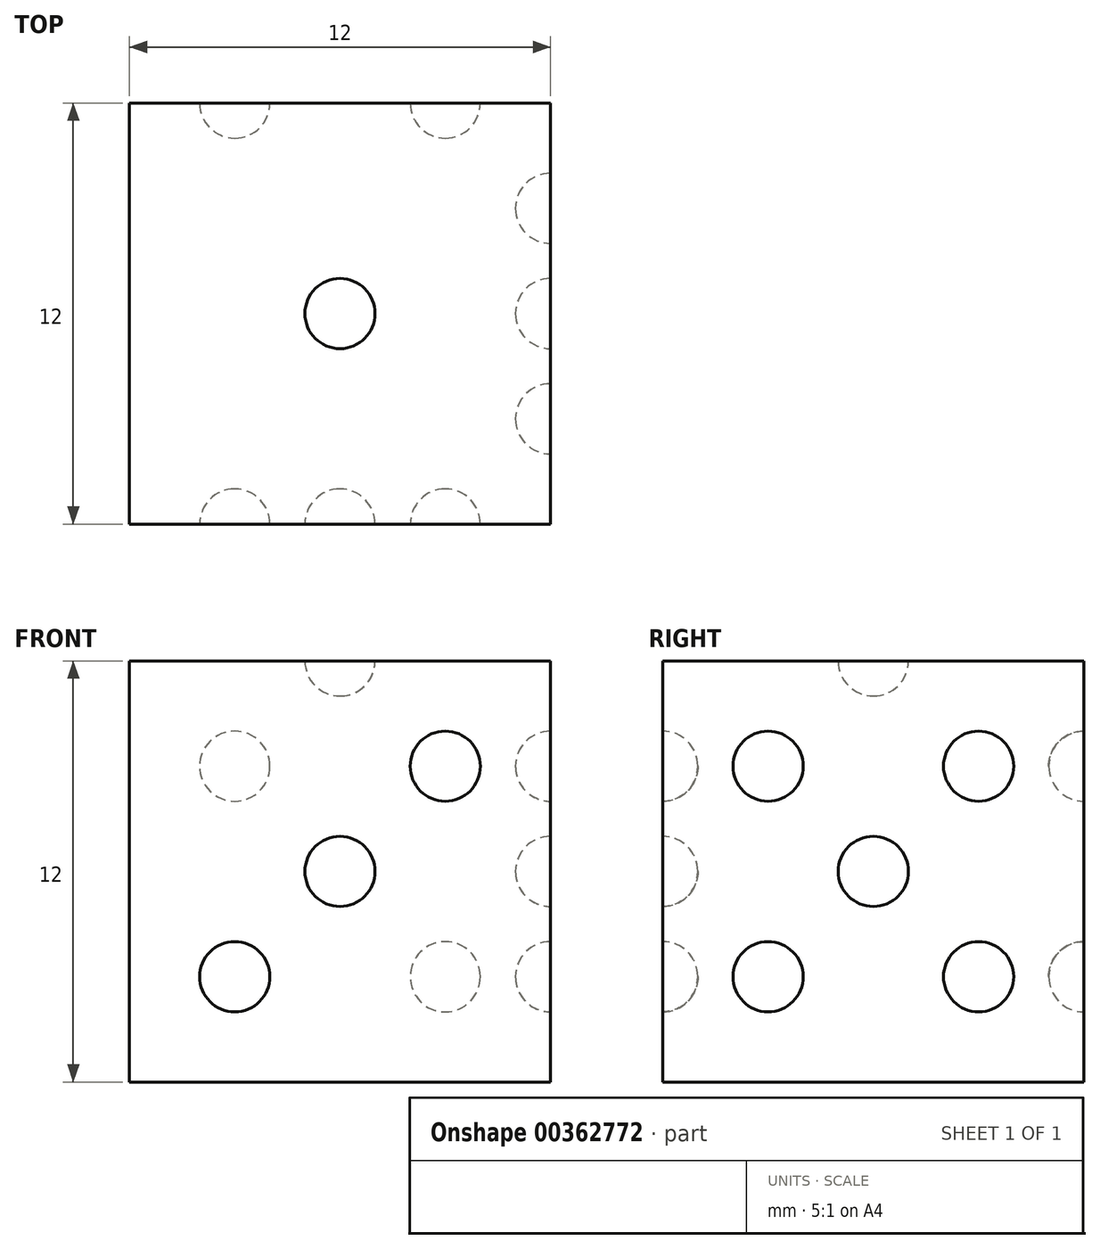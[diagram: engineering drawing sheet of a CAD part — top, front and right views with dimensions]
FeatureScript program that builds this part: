
annotation { "Feature Type Name" : "Feature", "Feature Type Description" : "" }
export const myFeature = defineFeature(function(context is Context, id is Id, definition is map)
    precondition{}
    {
        {
            var Q0;
            Q0=qCreatedBy(makeId("Top.planeOp"),FACE);
            cPlane(context, id + "F0", {"entities" : qUnion([Q0]), "cplaneType" : CPlaneType.OFFSET, "offset" : 6 * mm, "oppositeDirection" : true, "width" : 150 * mm, "height" : 150 * mm});
        }
        {
            var Q0;
            Q0=qCreatedBy(id+"F0.planeOp",FACE);
            var sketch = newSketch(context, id + "F1", { "sketchPlane" : qUnion([Q0])});
            skLineSegment(sketch, "E0.bottom", {"start": v(6, 6) * mm, "end": v(-6, 6) * mm});
            skLineSegment(sketch, "E0.top", {"start": v(6, -6) * mm, "end": v(-6, -6) * mm});
            skLineSegment(sketch, "E0.left", {"start": v(6, 6) * mm, "end": v(6, -6) * mm});
            skLineSegment(sketch, "E0.right", {"start": v(-6, 6) * mm, "end": v(-6, -6) * mm});
            skPoint(sketch, "E0.middle", {"position": v(0, 0) * mm});
            skSolve(sketch);
        }
        {
            var Q0;
            Q0=makeQuery(id+"F1.imprint","IMPRINT",FACE,{"disambiguationData":[TD([[makeQuery(id+"F1.imprint","IMPRINT",EDGE,{"derivedFrom":sQuery(id+"F1.wireOp",EDGE,"E0.bottom")}),1.0]])]});
            extrude(context, id + "F2", {"entities" : qUnion([Q0]), "depth" : 12 * mm});
        }
        {
            var Q0;
            Q0=makeQuery(id+"F2.opExtrude","CAP_FACE",FACE,{"disambiguationData":[OSD([sQuery(id+"F1.wireOp",EDGE,"E0.bottom"),sQuery(id+"F1.wireOp",EDGE,"E0.top"),sQuery(id+"F1.wireOp",EDGE,"E0.left"),sQuery(id+"F1.wireOp",EDGE,"E0.right")])],"isStart":false});
            var sketch = newSketch(context, id + "F3", { "sketchPlane" : qUnion([Q0])});
            skCircle(sketch, "E1", {"center": v(0, 0) * mm, "radius": 1 * mm});
            skSolve(sketch);
        }
        {
            var Q0;
            Q0=makeQuery(id+"F3.imprint","IMPRINT",FACE,{"disambiguationData":[TD([[makeQuery(id+"F3.imprint","IMPRINT",EDGE,{"derivedFrom":sQuery(id+"F3.wireOp",EDGE,"E1")}),1.0]])]});
            extrude(context, id + "F4", {"entities" : qUnion([Q0]), "operationType" : NewBodyOperationType.REMOVE, "oppositeDirection" : true, "depth" : 1 * mm});
        }
        {
            var Q0;
            Q0=makeQuery(id+"F4.boolean.opBoolean","COPY",EDGE,{"derivedFrom":makeQuery(id+"F4.opExtrude","CAP_EDGE",EDGE,{"disambiguationData":[OSD([sQuery(id+"F3.wireOp",EDGE,"E1")])],"isStart":false})});
            fillet(context, id + "F5", {"entities" : qUnion([Q0]), "radius" : 1 * mm, "tangentPropagation" : true, "allowEdgeOverflow" : false});
        }
        {
            var Q0;
            Q0=makeQuery(id+"F2.opExtrude","SWEPT_FACE",FACE,{"disambiguationData":[OSD([sQuery(id+"F1.wireOp",EDGE,"E0.top")])]});
            var sketch = newSketch(context, id + "F6", { "sketchPlane" : qUnion([Q0])});
            skCircle(sketch, "E2", {"center": v(0, 0) * mm, "radius": 1 * mm});
            skPoint(sketch, "E3", {"position": v(3, 3) * mm});
            skCircle(sketch, "E4", {"center": v(3, 3) * mm, "radius": 1 * mm});
            skPoint(sketch, "E5", {"position": v(-3, -3) * mm});
            skCircle(sketch, "E6", {"center": v(-3, -3) * mm, "radius": 1 * mm});
            skSolve(sketch);
        }
        {
            var Q0;
            Q0=makeQuery(id+"F6.imprint","IMPRINT",FACE,{"disambiguationData":[TD([[makeQuery(id+"F6.imprint","IMPRINT",EDGE,{"derivedFrom":sQuery(id+"F6.wireOp",EDGE,"E4")}),1.0]])]});
            var Q1;
            Q1=makeQuery(id+"F6.imprint","IMPRINT",FACE,{"disambiguationData":[TD([[makeQuery(id+"F6.imprint","IMPRINT",EDGE,{"derivedFrom":sQuery(id+"F6.wireOp",EDGE,"E2")}),1.0]])]});
            var Q2;
            Q2=makeQuery(id+"F6.imprint","IMPRINT",FACE,{"disambiguationData":[TD([[makeQuery(id+"F6.imprint","IMPRINT",EDGE,{"derivedFrom":sQuery(id+"F6.wireOp",EDGE,"E6")}),1.0]])]});
            extrude(context, id + "F7", {"entities" : qUnion([Q0, Q1, Q2]), "operationType" : NewBodyOperationType.REMOVE, "oppositeDirection" : true, "depth" : 1 * mm});
        }
        {
            var Q0;
            Q0=makeQuery(id+"F7.boolean.opBoolean","COPY",EDGE,{"derivedFrom":makeQuery(id+"F7.opExtrude","CAP_EDGE",EDGE,{"disambiguationData":[OSD([sQuery(id+"F6.wireOp",EDGE,"E4")])],"isStart":false})});
            var Q1;
            Q1=makeQuery(id+"F7.boolean.opBoolean","COPY",EDGE,{"derivedFrom":makeQuery(id+"F7.opExtrude","CAP_EDGE",EDGE,{"disambiguationData":[OSD([sQuery(id+"F6.wireOp",EDGE,"E2")])],"isStart":false})});
            var Q2;
            Q2=makeQuery(id+"F7.boolean.opBoolean","COPY",EDGE,{"derivedFrom":makeQuery(id+"F7.opExtrude","CAP_EDGE",EDGE,{"disambiguationData":[OSD([sQuery(id+"F6.wireOp",EDGE,"E6")])],"isStart":false})});
            fillet(context, id + "F8", {"entities" : qUnion([Q0, Q1, Q2]), "radius" : 1 * mm, "tangentPropagation" : true, "allowEdgeOverflow" : false});
        }
        {
            var Q0;
            Q0=makeQuery(id+"F2.opExtrude","SWEPT_FACE",FACE,{"disambiguationData":[OSD([sQuery(id+"F1.wireOp",EDGE,"E0.left")])]});
            var sketch = newSketch(context, id + "F9", { "sketchPlane" : qUnion([Q0])});
            skCircle(sketch, "E7", {"center": v(0, 0) * mm, "radius": 1 * mm});
            skPoint(sketch, "E8", {"position": v(3, 3) * mm});
            skPoint(sketch, "E9", {"position": v(-3, -3) * mm});
            skPoint(sketch, "E10", {"position": v(-3, 3) * mm});
            skPoint(sketch, "E11", {"position": v(3, -3) * mm});
            skCircle(sketch, "E12", {"center": v(-3, 3) * mm, "radius": 1 * mm});
            skCircle(sketch, "E13", {"center": v(3, 3) * mm, "radius": 1 * mm});
            skCircle(sketch, "E14", {"center": v(3, -3) * mm, "radius": 1 * mm});
            skCircle(sketch, "E15", {"center": v(-3, -3) * mm, "radius": 1 * mm});
            skSolve(sketch);
        }
        {
            var Q0;
            Q0=makeQuery(id+"F9.imprint","IMPRINT",FACE,{"disambiguationData":[TD([[makeQuery(id+"F9.imprint","IMPRINT",EDGE,{"derivedFrom":sQuery(id+"F9.wireOp",EDGE,"E12")}),1.0]])]});
            var Q1;
            Q1=makeQuery(id+"F9.imprint","IMPRINT",FACE,{"disambiguationData":[TD([[makeQuery(id+"F9.imprint","IMPRINT",EDGE,{"derivedFrom":sQuery(id+"F9.wireOp",EDGE,"E7")}),1.0]])]});
            var Q2;
            Q2=makeQuery(id+"F9.imprint","IMPRINT",FACE,{"disambiguationData":[TD([[makeQuery(id+"F9.imprint","IMPRINT",EDGE,{"derivedFrom":sQuery(id+"F9.wireOp",EDGE,"E13")}),1.0]])]});
            var Q3;
            Q3=makeQuery(id+"F9.imprint","IMPRINT",FACE,{"disambiguationData":[TD([[makeQuery(id+"F9.imprint","IMPRINT",EDGE,{"derivedFrom":sQuery(id+"F9.wireOp",EDGE,"E14")}),1.0]])]});
            var Q4;
            Q4=makeQuery(id+"F9.imprint","IMPRINT",FACE,{"disambiguationData":[TD([[makeQuery(id+"F9.imprint","IMPRINT",EDGE,{"derivedFrom":sQuery(id+"F9.wireOp",EDGE,"E15")}),1.0]])]});
            extrude(context, id + "F10", {"entities" : qUnion([Q0, Q1, Q2, Q3, Q4]), "operationType" : NewBodyOperationType.REMOVE, "oppositeDirection" : true, "depth" : 1 * mm});
        }
        {
            var Q0;
            Q0=makeQuery(id+"F10.boolean.opBoolean","COPY",EDGE,{"derivedFrom":makeQuery(id+"F10.opExtrude","CAP_EDGE",EDGE,{"disambiguationData":[OSD([sQuery(id+"F9.wireOp",EDGE,"E12")])],"isStart":false})});
            var Q1;
            Q1=makeQuery(id+"F10.boolean.opBoolean","COPY",EDGE,{"derivedFrom":makeQuery(id+"F10.opExtrude","CAP_EDGE",EDGE,{"disambiguationData":[OSD([sQuery(id+"F9.wireOp",EDGE,"E7")])],"isStart":false})});
            var Q2;
            Q2=makeQuery(id+"F10.boolean.opBoolean","COPY",EDGE,{"derivedFrom":makeQuery(id+"F10.opExtrude","CAP_EDGE",EDGE,{"disambiguationData":[OSD([sQuery(id+"F9.wireOp",EDGE,"E13")])],"isStart":false})});
            var Q3;
            Q3=makeQuery(id+"F10.boolean.opBoolean","COPY",EDGE,{"derivedFrom":makeQuery(id+"F10.opExtrude","CAP_EDGE",EDGE,{"disambiguationData":[OSD([sQuery(id+"F9.wireOp",EDGE,"E14")])],"isStart":false})});
            var Q4;
            Q4=makeQuery(id+"F10.boolean.opBoolean","COPY",EDGE,{"derivedFrom":makeQuery(id+"F10.opExtrude","CAP_EDGE",EDGE,{"disambiguationData":[OSD([sQuery(id+"F9.wireOp",EDGE,"E15")])],"isStart":false})});
            fillet(context, id + "F11", {"entities" : qUnion([Q0, Q1, Q2, Q3, Q4]), "radius" : 1 * mm, "tangentPropagation" : true, "allowEdgeOverflow" : false});
        }
        {
            var Q0;
            Q0=makeQuery(id+"F2.opExtrude","SWEPT_FACE",FACE,{"disambiguationData":[OSD([sQuery(id+"F1.wireOp",EDGE,"E0.bottom")])]});
            var sketch = newSketch(context, id + "F12", { "sketchPlane" : qUnion([Q0])});
            skCircle(sketch, "E16", {"center": v(-3, 3) * mm, "radius": 1 * mm});
            skCircle(sketch, "E17", {"center": v(3, 3) * mm, "radius": 1 * mm});
            skCircle(sketch, "E18", {"center": v(3, -3) * mm, "radius": 1 * mm});
            skCircle(sketch, "E19", {"center": v(-3, -3) * mm, "radius": 1 * mm});
            skSolve(sketch);
        }
        {
            var Q0;
            Q0=makeQuery(id+"F12.imprint","IMPRINT",FACE,{"disambiguationData":[TD([[makeQuery(id+"F12.imprint","IMPRINT",EDGE,{"derivedFrom":sQuery(id+"F12.wireOp",EDGE,"E16")}),1.0]])]});
            var Q1;
            Q1=makeQuery(id+"F12.imprint","IMPRINT",FACE,{"disambiguationData":[TD([[makeQuery(id+"F12.imprint","IMPRINT",EDGE,{"derivedFrom":sQuery(id+"F12.wireOp",EDGE,"E17")}),1.0]])]});
            var Q2;
            Q2=makeQuery(id+"F12.imprint","IMPRINT",FACE,{"disambiguationData":[TD([[makeQuery(id+"F12.imprint","IMPRINT",EDGE,{"derivedFrom":sQuery(id+"F12.wireOp",EDGE,"E18")}),1.0]])]});
            var Q3;
            Q3=makeQuery(id+"F12.imprint","IMPRINT",FACE,{"disambiguationData":[TD([[makeQuery(id+"F12.imprint","IMPRINT",EDGE,{"derivedFrom":sQuery(id+"F12.wireOp",EDGE,"E19")}),1.0]])]});
            extrude(context, id + "F13", {"entities" : qUnion([Q0, Q1, Q2, Q3]), "operationType" : NewBodyOperationType.REMOVE, "oppositeDirection" : true, "depth" : 1 * mm});
        }
        {
            var Q0;
            Q0=makeQuery(id+"F13.boolean.opBoolean","COPY",EDGE,{"derivedFrom":makeQuery(id+"F13.opExtrude","CAP_EDGE",EDGE,{"disambiguationData":[OSD([sQuery(id+"F12.wireOp",EDGE,"E16")])],"isStart":false})});
            var Q1;
            Q1=makeQuery(id+"F13.boolean.opBoolean","COPY",EDGE,{"derivedFrom":makeQuery(id+"F13.opExtrude","CAP_EDGE",EDGE,{"disambiguationData":[OSD([sQuery(id+"F12.wireOp",EDGE,"E17")])],"isStart":false})});
            var Q2;
            Q2=makeQuery(id+"F13.boolean.opBoolean","COPY",EDGE,{"derivedFrom":makeQuery(id+"F13.opExtrude","CAP_EDGE",EDGE,{"disambiguationData":[OSD([sQuery(id+"F12.wireOp",EDGE,"E19")])],"isStart":false})});
            var Q3;
            Q3=makeQuery(id+"F13.boolean.opBoolean","COPY",EDGE,{"derivedFrom":makeQuery(id+"F13.opExtrude","CAP_EDGE",EDGE,{"disambiguationData":[OSD([sQuery(id+"F12.wireOp",EDGE,"E18")])],"isStart":false})});
            fillet(context, id + "F14", {"entities" : qUnion([Q0, Q1, Q2, Q3]), "radius" : 1 * mm, "tangentPropagation" : true, "allowEdgeOverflow" : false});
        }
    });
